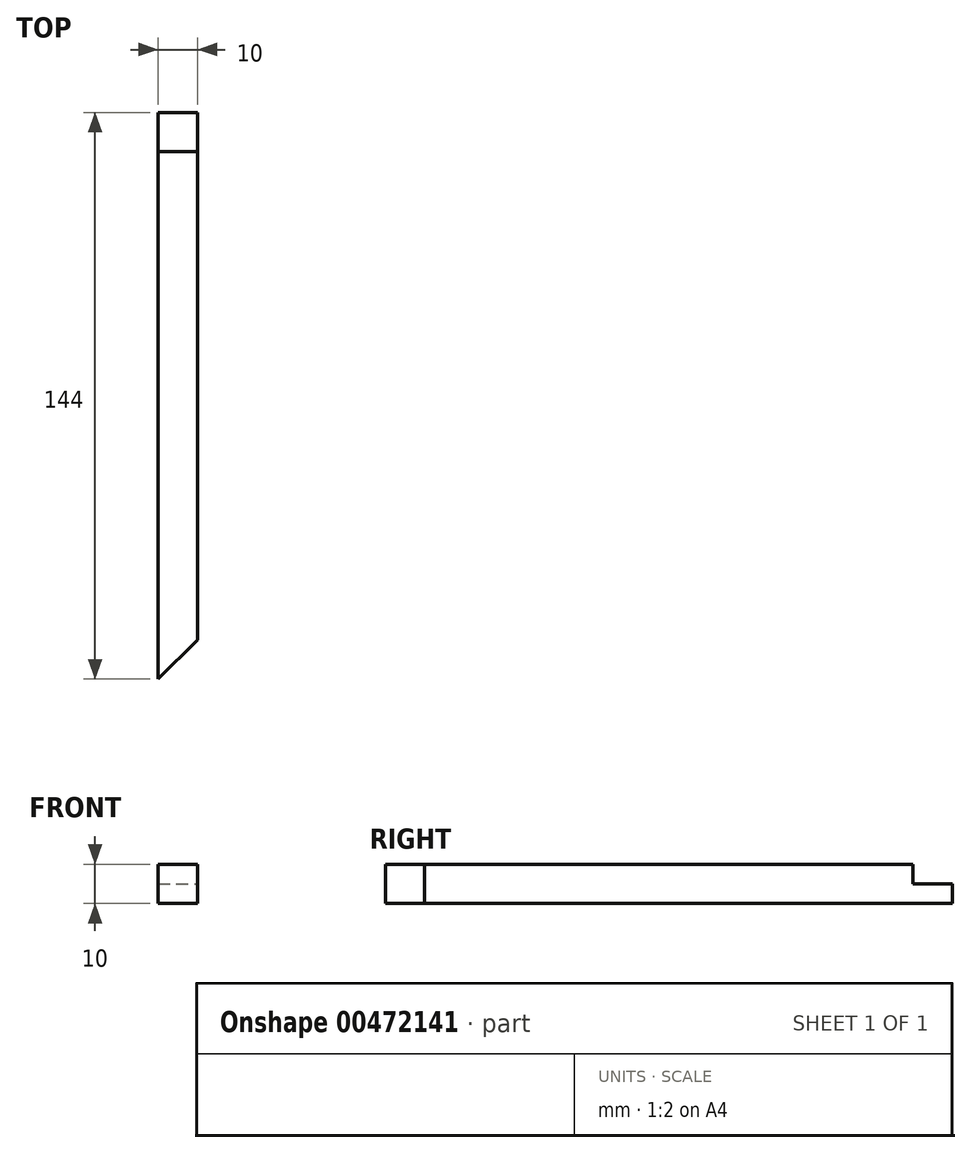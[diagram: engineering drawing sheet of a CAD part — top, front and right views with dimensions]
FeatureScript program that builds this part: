
annotation { "Feature Type Name" : "Feature", "Feature Type Description" : "" }
export const myFeature = defineFeature(function(context is Context, id is Id, definition is map)
    precondition{}
    {
        {
            var Q0;
            Q0=qCreatedBy(makeId("Front.planeOp"),FACE);
            var sketch = newSketch(context, id + "F0", { "sketchPlane" : qUnion([Q0])});
            skLineSegment(sketch, "E0.bottom", {"start": v(5, -5) * mm, "end": v(-5, -5) * mm});
            skLineSegment(sketch, "E0.top", {"start": v(5, 5) * mm, "end": v(-5, 5) * mm});
            skLineSegment(sketch, "E0.left", {"start": v(5, -5) * mm, "end": v(5, 5) * mm});
            skLineSegment(sketch, "E0.right", {"start": v(-5, -5) * mm, "end": v(-5, 5) * mm});
            skPoint(sketch, "E0.middle", {"position": v(0, 0) * mm});
            skSolve(sketch);
        }
        {
            var Q0;
            Q0=makeQuery(id+"F0.imprint","IMPRINT",FACE,{"disambiguationData":[TD([[makeQuery(id+"F0.imprint","IMPRINT",EDGE,{"derivedFrom":sQuery(id+"F0.wireOp",EDGE,"E0.bottom")}),-1.0]])]});
            extrude(context, id + "F1", {"entities" : qUnion([Q0]), "depth" : 144 * mm});
        }
        {
            var Q0;
            Q0=makeQuery(id+"F1.opExtrude","SWEPT_FACE",FACE,{"disambiguationData":[OSD([sQuery(id+"F0.wireOp",EDGE,"E0.left")])]});
            var sketch = newSketch(context, id + "F2", { "sketchPlane" : qUnion([Q0])});
            skLineSegment(sketch, "E1", {"start": v(-134, 5) * mm, "end": v(-134, 0) * mm});
            skLineSegment(sketch, "E2", {"start": v(-134, 0) * mm, "end": v(-144, 0) * mm});
            skLineSegment(sketch, "E3", {"start": v(-10, 5) * mm, "end": v(-10, 0) * mm});
            skLineSegment(sketch, "E4", {"start": v(-10, 0) * mm, "end": v(0, 0) * mm});
            skSolve(sketch);
        }
        {
            var Q0;
            {var subQ0=sQuery(id+"F2.wireOp",EDGE,"E3");Q0=makeQuery(id+"F2.imprint","IMPRINT",FACE,{"disambiguationData":[TD([[makeQuery(id+"F2.imprint","IMPRINT",EDGE,{"derivedFrom":subQ0}),1.0]])]});}
            extrude(context, id + "F3", {"entities" : qUnion([Q0]), "operationType" : NewBodyOperationType.REMOVE, "oppositeDirection" : true, "depth" : 10 * mm});
        }
        {
            var Q0;
            Q0=makeQuery(id+"F1.opExtrude","CAP_EDGE",EDGE,{"disambiguationData":[OSD([sQuery(id+"F0.wireOp",EDGE,"E0.left")])],"isStart":false});
            chamfer(context, id + "F4", {"entities" : qUnion([Q0]), "width" : 10 * mm, "tangentPropagation" : true});
        }
    });
